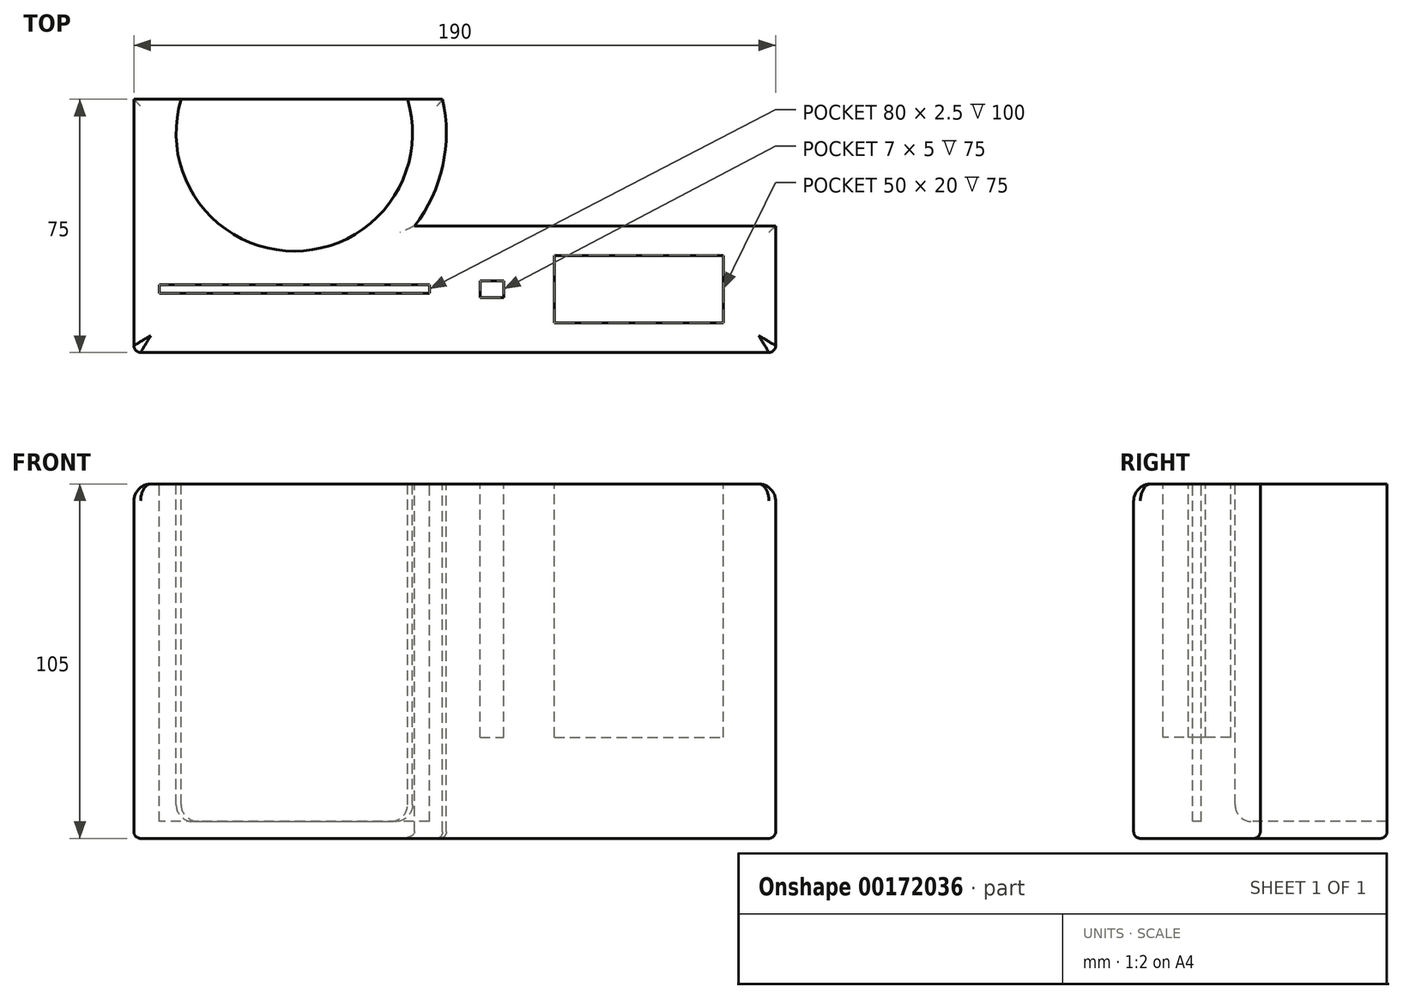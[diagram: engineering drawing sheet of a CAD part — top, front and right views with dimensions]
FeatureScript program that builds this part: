
annotation { "Feature Type Name" : "Feature", "Feature Type Description" : "" }
export const myFeature = defineFeature(function(context is Context, id is Id, definition is map)
    precondition{}
    {
        {
            var Q0;
            Q0=qCreatedBy(makeId("Right.planeOp"),FACE);
            var sketch = newSketch(context, id + "F0", { "sketchPlane" : qUnion([Q0])});
            skLineSegment(sketch, "E0.bottom", {"start": v(37.5, 52.5) * mm, "end": v(-37.5, 52.5) * mm});
            skLineSegment(sketch, "E0.top", {"start": v(37.5, -52.5) * mm, "end": v(-37.5, -52.5) * mm});
            skLineSegment(sketch, "E0.left", {"start": v(37.5, 52.5) * mm, "end": v(37.5, -52.5) * mm});
            skLineSegment(sketch, "E0.right", {"start": v(-37.5, 52.5) * mm, "end": v(-37.5, -52.5) * mm});
            skPoint(sketch, "E0.middle", {"position": v(0, 0) * mm});
            skSolve(sketch);
        }
        {
            var Q0;
            Q0 = qSketchRegion(id + "F0", true);
            extrude(context, id + "F1", {"entities" : qUnion([Q0]), "endBound" : BoundingType.SYMMETRIC, "depth" : 190 * mm});
        }
        {
            var Q0;
            Q0=makeQuery(id+"F1.opExtrude","SWEPT_FACE",FACE,{"disambiguationData":[OSD([sQuery(id+"F0.wireOp",EDGE,"E0.bottom")])]});
            var sketch = newSketch(context, id + "F2", { "sketchPlane" : qUnion([Q0])});
            skLineSegment(sketch, "E1.bottom", {"start": v(-7.5, -17.5) * mm, "end": v(-87.5, -17.5) * mm});
            skLineSegment(sketch, "E1.top", {"start": v(-7.5, -20) * mm, "end": v(-87.5, -20) * mm});
            skLineSegment(sketch, "E1.left", {"start": v(-7.5, -17.5) * mm, "end": v(-7.5, -20) * mm});
            skLineSegment(sketch, "E1.right", {"start": v(-87.5, -17.5) * mm, "end": v(-87.5, -20) * mm});
            skPoint(sketch, "E1.middle", {"position": v(-47.5, -18.75) * mm});
            skLineSegment(sketch, "E2", {"start": v(0, 0) * mm, "end": v(0, -18.75) * mm, "construction": true});
            skLineSegment(sketch, "E3", {"start": v(0, -18.75) * mm, "end": v(0, -37.5) * mm, "construction": true});
            skLineSegment(sketch, "E4", {"start": v(-87.5, -20) * mm, "end": v(-95, -20) * mm, "construction": true});
            skLineSegment(sketch, "E5", {"start": v(-7.5, -20) * mm, "end": v(0, -20) * mm, "construction": true});
            skSolve(sketch);
        }
        {
            var Q0;
            Q0 = qSketchRegion(id + "F2", true);
            extrude(context, id + "F3", {"entities" : qUnion([Q0]), "operationType" : NewBodyOperationType.REMOVE, "oppositeDirection" : true, "depth" : 100 * mm});
        }
        {
            var Q0;
            Q0=makeQuery(id+"F1.opExtrude","SWEPT_FACE",FACE,{"disambiguationData":[OSD([sQuery(id+"F0.wireOp",EDGE,"E0.bottom")])]});
            var sketch = newSketch(context, id + "F4", { "sketchPlane" : qUnion([Q0])});
            skLineSegment(sketch, "E6.bottom", {"start": v(7.5, -16.25) * mm, "end": v(14.5, -16.25) * mm});
            skLineSegment(sketch, "E6.top", {"start": v(7.5, -21.25) * mm, "end": v(14.5, -21.25) * mm});
            skLineSegment(sketch, "E6.left", {"start": v(7.5, -16.25) * mm, "end": v(7.5, -21.25) * mm});
            skLineSegment(sketch, "E6.right", {"start": v(14.5, -16.25) * mm, "end": v(14.5, -21.25) * mm});
            skPoint(sketch, "E6.middle", {"position": v(11, -18.75) * mm});
            skPoint(sketch, "E7", {"position": v(7.5, -18.75) * mm});
            skPoint(sketch, "E8", {"position": v(-7.5, -18.75) * mm});
            skLineSegment(sketch, "E9", {"start": v(-7.5, -18.75) * mm, "end": v(7.5, -18.75) * mm, "construction": true});
            skPoint(sketch, "E10", {"position": v(0, -18.75) * mm});
            skSolve(sketch);
        }
        {
            var Q0;
            Q0 = qSketchRegion(id + "F4", true);
            extrude(context, id + "F5", {"entities" : qUnion([Q0]), "operationType" : NewBodyOperationType.REMOVE, "oppositeDirection" : true, "depth" : 75 * mm});
        }
        {
            var Q0;
            Q0=makeQuery(id+"F1.opExtrude","SWEPT_FACE",FACE,{"disambiguationData":[OSD([sQuery(id+"F0.wireOp",EDGE,"E0.bottom")])]});
            var sketch = newSketch(context, id + "F6", { "sketchPlane" : qUnion([Q0])});
            skLineSegment(sketch, "E11.bottom", {"start": v(29.5, -8.75) * mm, "end": v(79.5, -8.75) * mm});
            skLineSegment(sketch, "E11.top", {"start": v(29.5, -28.75) * mm, "end": v(79.5, -28.75) * mm});
            skLineSegment(sketch, "E11.left", {"start": v(29.5, -8.75) * mm, "end": v(29.5, -28.75) * mm});
            skLineSegment(sketch, "E11.right", {"start": v(79.5, -8.75) * mm, "end": v(79.5, -28.75) * mm});
            skPoint(sketch, "E11.middle", {"position": v(54.5, -18.75) * mm});
            skPoint(sketch, "E12", {"position": v(29.5, -18.75) * mm});
            skPoint(sketch, "E13", {"position": v(14.5, -18.75) * mm});
            skLineSegment(sketch, "E14", {"start": v(29.5, -18.75) * mm, "end": v(14.5, -18.75) * mm, "construction": true});
            skLineSegment(sketch, "E15", {"start": v(7.5, -18.75) * mm, "end": v(-7.5, -18.75) * mm, "construction": true});
            skSolve(sketch);
        }
        {
            var Q0;
            Q0 = qSketchRegion(id + "F6", true);
            extrude(context, id + "F7", {"entities" : qUnion([Q0]), "operationType" : NewBodyOperationType.REMOVE, "oppositeDirection" : true, "depth" : 75 * mm});
        }
        {
            var Q0;
            Q0=makeQuery(id+"F1.opExtrude","SWEPT_FACE",FACE,{"disambiguationData":[OSD([sQuery(id+"F0.wireOp",EDGE,"E0.bottom")])]});
            var sketch = newSketch(context, id + "F8", { "sketchPlane" : qUnion([Q0])});
            skCircle(sketch, "E16", {"center": v(-47.5, 27.5) * mm, "radius": 35 * mm});
            skSolve(sketch);
        }
        {
            var Q0;
            Q0 = qSketchRegion(id + "F8", true);
            extrude(context, id + "F9", {"entities" : qUnion([Q0]), "operationType" : NewBodyOperationType.REMOVE, "oppositeDirection" : true, "depth" : 100 * mm});
        }
        {
            var Q0;
            Q0=makeQuery(id+"F1.opExtrude","SWEPT_FACE",FACE,{"disambiguationData":[OSD([sQuery(id+"F0.wireOp",EDGE,"E0.bottom")])]});
            var sketch = newSketch(context, id + "F10", { "sketchPlane" : qUnion([Q0])});
            skLineSegment(sketch, "E17", {"start": v(95, 37.5) * mm, "end": v(95, 0) * mm});
            skLineSegment(sketch, "E18", {"start": v(95, 0) * mm, "end": v(-11.88, 0) * mm});
            skArc(sketch, "E19", {"start": v(-11.88, 0) * mm, "mid": v(-3.55, 17.83) * mm, "end": v(-3.63, 37.5) * mm});
            skLineSegment(sketch, "E20", {"start": v(95, 37.5) * mm, "end": v(-3.63, 37.5) * mm});
            skLineSegment(sketch, "E21", {"start": v(79.5, 0) * mm, "end": v(79.5, -8.75) * mm, "construction": true});
            skLineSegment(sketch, "E22", {"start": v(79.5, -28.75) * mm, "end": v(79.5, -37.5) * mm, "construction": true});
            skSolve(sketch);
        }
        {
            var Q0;
            Q0 = qSketchRegion(id + "F10", true);
            extrude(context, id + "F11", {"entities" : qUnion([Q0]), "operationType" : NewBodyOperationType.REMOVE, "endBound" : BoundingType.THROUGH_ALL, "oppositeDirection" : true, "depth" : 25 * mm});
        }
        {
            var Q0;
            Q0=makeQuery(id+"F9.boolean.opBoolean","COPY",EDGE,{"derivedFrom":makeQuery(id+"F9.opExtrude","CAP_EDGE",EDGE,{"disambiguationData":[OSD([sQuery(id+"F8.wireOp",EDGE,"E16")])],"isStart":false})});
            var Q1;
            Q1=makeQuery(id+"F9.boolean.opBoolean","COPY",EDGE,{"derivedFrom":makeQuery(id+"F9.opExtrude","CAP_EDGE",EDGE,{"disambiguationData":[OSD([sQuery(id+"F8.wireOp",EDGE,"E16")])],"isStart":true})});
            var Q2;
            Q2=makeQuery(id+"F11.boolean.opBoolean","COPY",EDGE,{"derivedFrom":makeQuery(id+"F11.opExtrude","CAP_EDGE",EDGE,{"disambiguationData":[OSD([sQuery(id+"F10.wireOp",EDGE,"E19")])],"isStart":true})});
            var Q3;
            Q3=makeQuery(id+"F11.boolean.opBoolean","COPY",EDGE,{"derivedFrom":makeQuery(id+"F11.opExtrude","CAP_EDGE",EDGE,{"disambiguationData":[OSD([sQuery(id+"F10.wireOp",EDGE,"E18")])],"isStart":true})});
            var Q4;
            Q4=makeQuery(id+"F1.opExtrude","CAP_EDGE",EDGE,{"disambiguationData":[OSD([sQuery(id+"F0.wireOp",EDGE,"E0.bottom")])],"isStart":false});
            var Q5;
            Q5=makeQuery(id+"F1.opExtrude","SWEPT_EDGE",EDGE,{"disambiguationData":[OSD([sQuery(id+"F0.wireOp",EDGE,"E0.bottom"),sQuery(id+"F0.wireOp",EDGE,"E0.right")])]});
            var Q6;
            Q6=makeQuery(id+"F1.opExtrude","CAP_EDGE",EDGE,{"disambiguationData":[OSD([sQuery(id+"F0.wireOp",EDGE,"E0.bottom")])],"isStart":true});
            fillet(context, id + "F12", {"entities" : qUnion([Q0, Q1, Q2, Q3, Q4, Q5, Q6]), "radius" : 5 * mm, "tangentPropagation" : true, "allowEdgeOverflow" : false});
        }
        {
            var Q0;
            Q0=makeQuery(id+"F7.boolean.opBoolean","COPY",EDGE,{"derivedFrom":makeQuery(id+"F7.opExtrude","CAP_EDGE",EDGE,{"disambiguationData":[OSD([sQuery(id+"F6.wireOp",EDGE,"E11.top")])],"isStart":true})});
            var Q1;
            Q1=makeQuery(id+"F7.boolean.opBoolean","COPY",EDGE,{"derivedFrom":makeQuery(id+"F7.opExtrude","CAP_EDGE",EDGE,{"disambiguationData":[OSD([sQuery(id+"F6.wireOp",EDGE,"E11.right")])],"isStart":true})});
            var Q2;
            Q2=makeQuery(id+"F7.boolean.opBoolean","COPY",EDGE,{"derivedFrom":makeQuery(id+"F7.opExtrude","CAP_EDGE",EDGE,{"disambiguationData":[OSD([sQuery(id+"F6.wireOp",EDGE,"E11.bottom")])],"isStart":true})});
            var Q3;
            Q3=makeQuery(id+"F7.boolean.opBoolean","COPY",EDGE,{"derivedFrom":makeQuery(id+"F7.opExtrude","CAP_EDGE",EDGE,{"disambiguationData":[OSD([sQuery(id+"F6.wireOp",EDGE,"E11.left")])],"isStart":true})});
            var Q4;
            Q4=makeQuery(id+"F5.boolean.opBoolean","COPY",EDGE,{"derivedFrom":makeQuery(id+"F5.opExtrude","CAP_EDGE",EDGE,{"disambiguationData":[OSD([sQuery(id+"F4.wireOp",EDGE,"E6.bottom")])],"isStart":true})});
            var Q5;
            Q5=makeQuery(id+"F5.boolean.opBoolean","COPY",EDGE,{"derivedFrom":makeQuery(id+"F5.opExtrude","CAP_EDGE",EDGE,{"disambiguationData":[OSD([sQuery(id+"F4.wireOp",EDGE,"E6.left")])],"isStart":true})});
            var Q6;
            Q6=makeQuery(id+"F5.boolean.opBoolean","COPY",EDGE,{"derivedFrom":makeQuery(id+"F5.opExtrude","CAP_EDGE",EDGE,{"disambiguationData":[OSD([sQuery(id+"F4.wireOp",EDGE,"E6.top")])],"isStart":true})});
            var Q7;
            Q7=makeQuery(id+"F5.boolean.opBoolean","COPY",EDGE,{"derivedFrom":makeQuery(id+"F5.opExtrude","CAP_EDGE",EDGE,{"disambiguationData":[OSD([sQuery(id+"F4.wireOp",EDGE,"E6.right")])],"isStart":true})});
            var Q8;
            Q8=makeQuery(id+"F3.boolean.opBoolean","COPY",EDGE,{"derivedFrom":makeQuery(id+"F3.opExtrude","CAP_EDGE",EDGE,{"disambiguationData":[OSD([sQuery(id+"F2.wireOp",EDGE,"E1.left")])],"isStart":true})});
            var Q9;
            Q9=makeQuery(id+"F3.boolean.opBoolean","COPY",EDGE,{"derivedFrom":makeQuery(id+"F3.opExtrude","CAP_EDGE",EDGE,{"disambiguationData":[OSD([sQuery(id+"F2.wireOp",EDGE,"E1.top")])],"isStart":true})});
            var Q10;
            Q10=makeQuery(id+"F3.boolean.opBoolean","COPY",EDGE,{"derivedFrom":makeQuery(id+"F3.opExtrude","CAP_EDGE",EDGE,{"disambiguationData":[OSD([sQuery(id+"F2.wireOp",EDGE,"E1.bottom")])],"isStart":true})});
            var Q11;
            Q11=makeQuery(id+"F3.boolean.opBoolean","COPY",EDGE,{"derivedFrom":makeQuery(id+"F3.opExtrude","CAP_EDGE",EDGE,{"disambiguationData":[OSD([sQuery(id+"F2.wireOp",EDGE,"E1.right")])],"isStart":true})});
            var Q12;
            Q12=makeQuery(id+"F11.boolean.opBoolean","COPY",EDGE,{"derivedFrom":makeQuery(id+"F11.opExtrude","SWEPT_EDGE",EDGE,{"disambiguationData":[OSD([sQuery(id+"F0.wireOp",EDGE,"E0.bottom"),sQuery(id+"F0.wireOp",EDGE,"E0.left"),sQuery(id+"F10.wireOp",EDGE,"E19"),sQuery(id+"F10.wireOp",EDGE,"E20")])]})});
            var Q13;
            Q13=makeQuery(id+"F1.opExtrude","CAP_EDGE",EDGE,{"disambiguationData":[OSD([sQuery(id+"F0.wireOp",EDGE,"E0.right")])],"isStart":true});
            var Q14;
            Q14=makeQuery(id+"F1.opExtrude","CAP_EDGE",EDGE,{"disambiguationData":[OSD([sQuery(id+"F0.wireOp",EDGE,"E0.right")])],"isStart":false});
            var Q15;
            Q15=makeQuery(id+"F1.opExtrude","SWEPT_FACE",FACE,{"disambiguationData":[OSD([sQuery(id+"F0.wireOp",EDGE,"E0.top")])]});
            fillet(context, id + "F13", {"entities" : qUnion([Q0, Q1, Q2, Q3, Q4, Q5, Q6, Q7, Q8, Q9, Q10, Q11, Q12, Q13, Q14, Q15]), "radius" : 2 * mm, "tangentPropagation" : true, "allowEdgeOverflow" : false});
        }
    });
